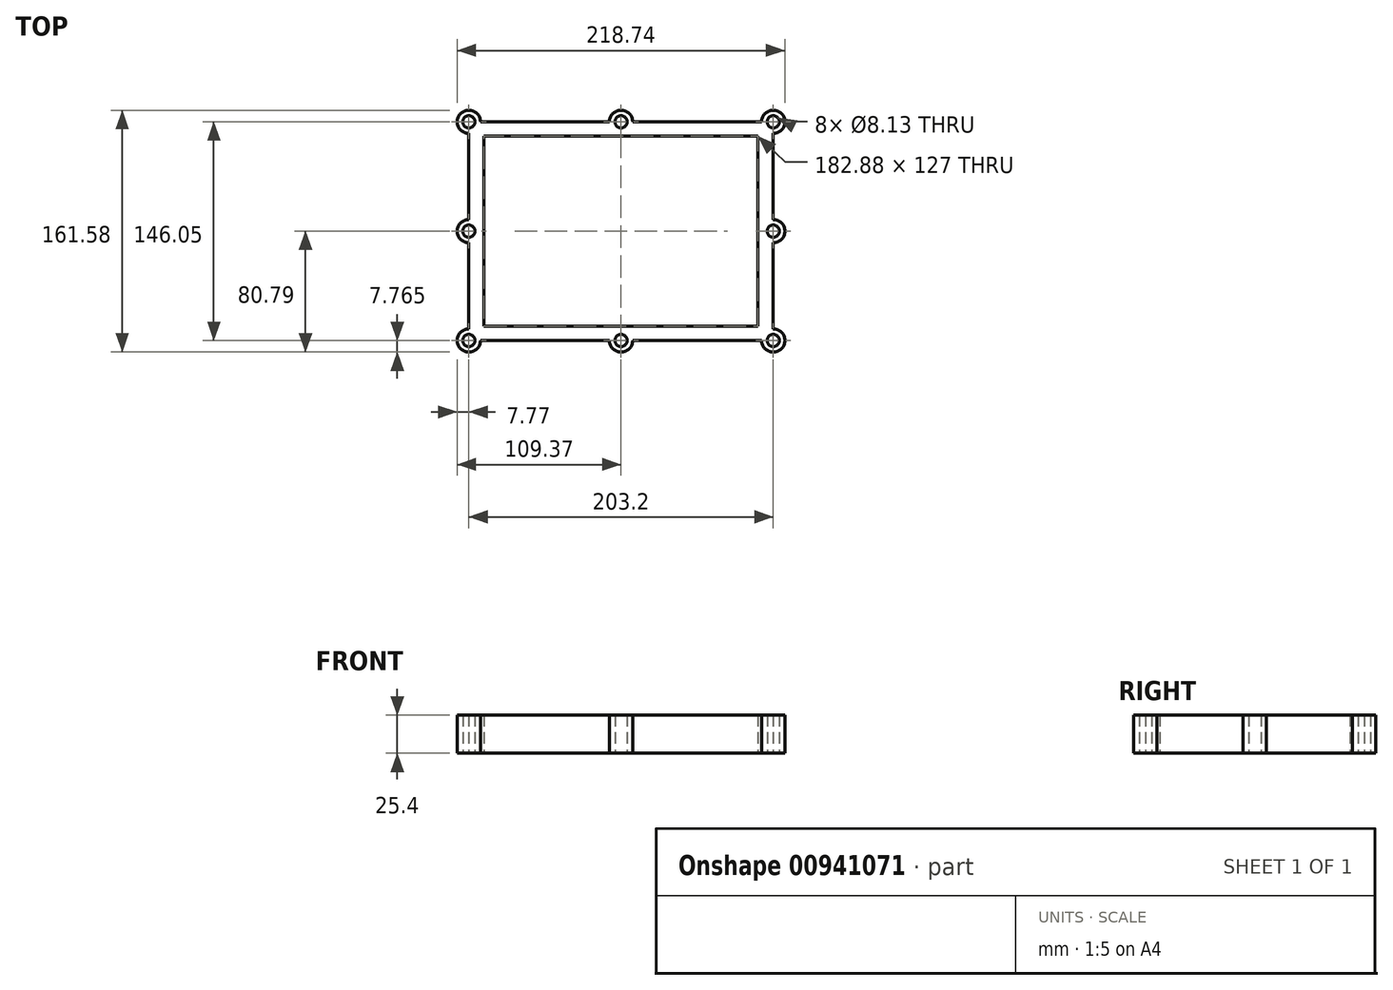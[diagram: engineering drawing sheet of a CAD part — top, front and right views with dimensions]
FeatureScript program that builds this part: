
annotation { "Feature Type Name" : "Feature", "Feature Type Description" : "" }
export const myFeature = defineFeature(function(context is Context, id is Id, definition is map)
    precondition{}
    {
        {
            var Q0;
            Q0=qCreatedBy(makeId("Top.planeOp"),FACE);
            var sketch = newSketch(context, id + "F0", { "sketchPlane" : qUnion([Q0])});
            skLineSegment(sketch, "E0.bottom", {"start": v(-101.6, 73.03) * mm, "end": v(101.6, 73.03) * mm});
            skLineSegment(sketch, "E0.top", {"start": v(-101.6, -73.03) * mm, "end": v(101.6, -73.03) * mm});
            skLineSegment(sketch, "E0.left", {"start": v(-101.6, 73.02) * mm, "end": v(-101.6, -73.03) * mm});
            skLineSegment(sketch, "E0.right", {"start": v(101.6, 73.03) * mm, "end": v(101.6, -73.02) * mm});
            skLineSegment(sketch, "E1", {"start": v(-101.6, 0) * mm, "end": v(101.6, 0) * mm, "construction": true});
            skLineSegment(sketch, "E2", {"start": v(0, 73.03) * mm, "end": v(0, -73.03) * mm, "construction": true});
            skPoint(sketch, "E2.startSnap0", {"position": v(0, 73.02) * mm});
            skCircle(sketch, "E3", {"center": v(101.6, -73.03) * mm, "radius": 7.77 * mm});
            skCircle(sketch, "E4", {"center": v(101.6, -73.03) * mm, "radius": 4.06 * mm});
            skCircle(sketch, "E5", {"center": v(101.6, 0) * mm, "radius": 7.77 * mm});
            skCircle(sketch, "E6", {"center": v(101.6, 0) * mm, "radius": 4.06 * mm});
            skCircle(sketch, "E7", {"center": v(101.6, 73.03) * mm, "radius": 7.77 * mm});
            skCircle(sketch, "E8", {"center": v(101.6, 73.03) * mm, "radius": 4.06 * mm});
            skCircle(sketch, "E9", {"center": v(0, 73.03) * mm, "radius": 7.77 * mm});
            skCircle(sketch, "E10", {"center": v(0, 73.03) * mm, "radius": 4.06 * mm});
            skCircle(sketch, "E11", {"center": v(-101.6, 73.03) * mm, "radius": 7.77 * mm});
            skCircle(sketch, "E12", {"center": v(-101.6, 73.03) * mm, "radius": 4.06 * mm});
            skCircle(sketch, "E13", {"center": v(-101.6, 0) * mm, "radius": 7.77 * mm});
            skCircle(sketch, "E14", {"center": v(-101.6, 0) * mm, "radius": 4.06 * mm});
            skCircle(sketch, "E15", {"center": v(-101.6, -73.03) * mm, "radius": 7.77 * mm});
            skCircle(sketch, "E16", {"center": v(-101.6, -73.03) * mm, "radius": 4.06 * mm});
            skCircle(sketch, "E17", {"center": v(0, -73.03) * mm, "radius": 7.77 * mm});
            skCircle(sketch, "E18", {"center": v(0, -73.03) * mm, "radius": 4.06 * mm});
            skLineSegment(sketch, "E19", {"start": v(-91.44, -63.5) * mm, "end": v(91.44, -63.5) * mm});
            skLineSegment(sketch, "E20", {"start": v(91.44, 63.5) * mm, "end": v(91.44, -63.5) * mm});
            skLineSegment(sketch, "E21", {"start": v(-91.44, 63.5) * mm, "end": v(-91.44, -63.5) * mm});
            skLineSegment(sketch, "E22", {"start": v(91.44, -63.5) * mm, "end": v(91.44, -73.03) * mm, "construction": true});
            skLineSegment(sketch, "E23", {"start": v(91.44, -24.5) * mm, "end": v(101.6, -24.5) * mm, "construction": true});
            skLineSegment(sketch, "E24", {"start": v(-91.44, 63.5) * mm, "end": v(91.44, 63.5) * mm});
            skSolve(sketch);
        }
        {
            var Q0;
            Q0 = qSketchRegion(id + "F0", true);
            extrude(context, id + "F1", {"entities" : qUnion([Q0]), "depth" : 25.4 * mm, "offsetDistance" : 25.4 * mm});
        }
    });
